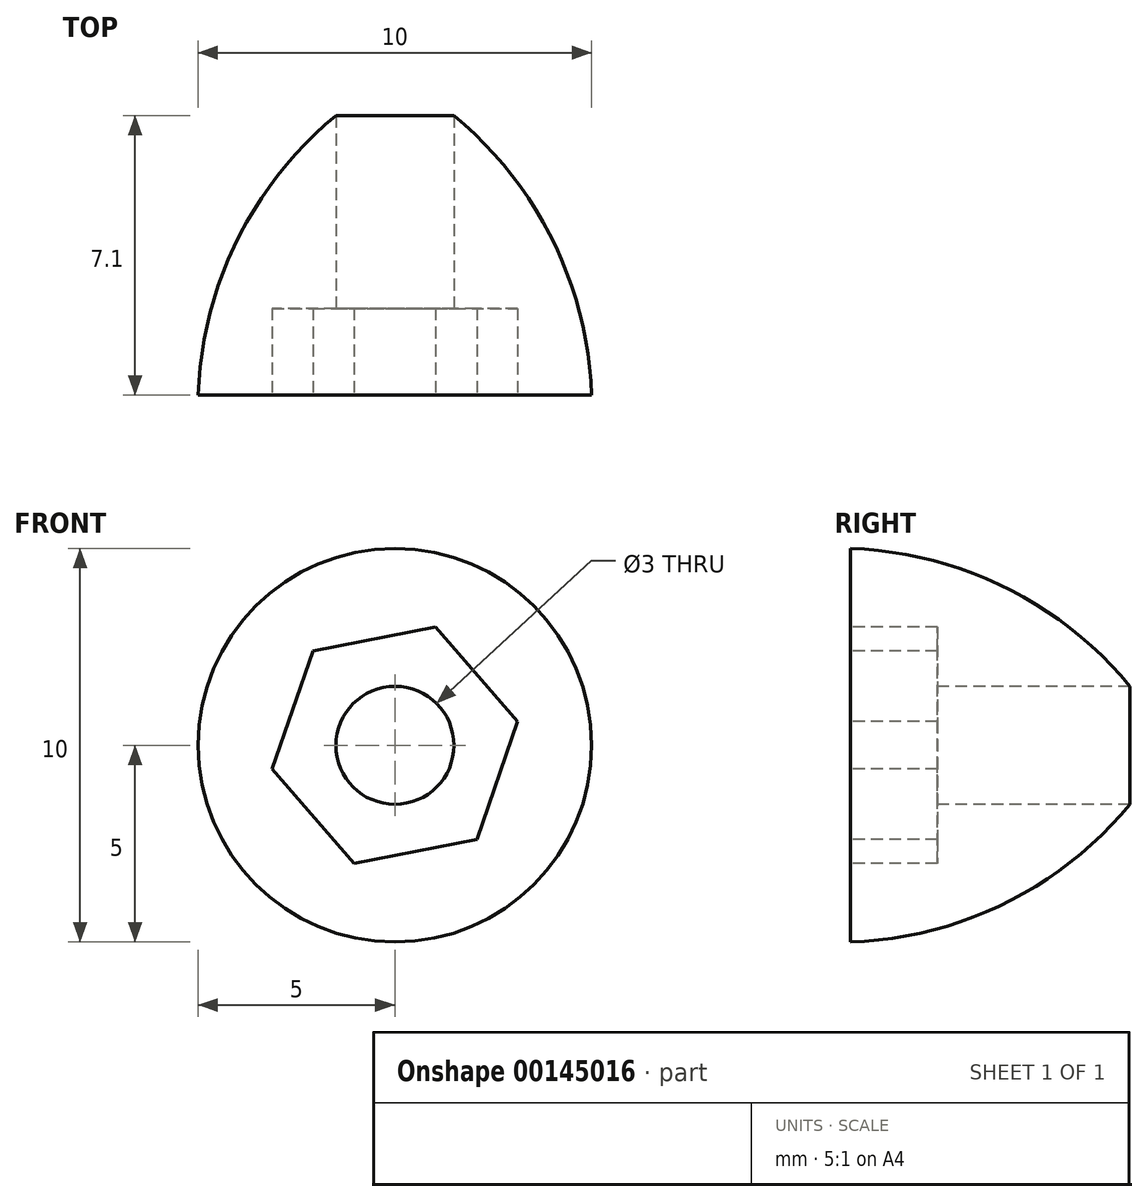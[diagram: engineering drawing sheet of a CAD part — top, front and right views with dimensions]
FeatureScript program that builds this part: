
annotation { "Feature Type Name" : "Feature", "Feature Type Description" : "" }
export const myFeature = defineFeature(function(context is Context, id is Id, definition is map)
    precondition{}
    {
        {
            var Q0;
            Q0=qCreatedBy(makeId("Top.planeOp"),FACE);
            var sketch = newSketch(context, id + "F0", { "sketchPlane" : qUnion([Q0])});
            skLineSegment(sketch, "E0", {"start": v(0, 0) * mm, "end": v(0, 8.12) * mm});
            skLineSegment(sketch, "E1", {"start": v(5, 0) * mm, "end": v(0, 0) * mm});
            skArc(sketch, "E2", {"start": v(5, 0) * mm, "mid": v(3.57, 4.72) * mm, "end": v(0, 8.12) * mm});
            skSolve(sketch);
        }
        {
            var Q0;
            Q0 = qSketchRegion(id + "F0", true);
            var Q1;
            Q1=sQuery(id+"F0.wireOp",EDGE,"E0");
            revolve(context, id + "F1", {"entities" : qUnion([Q0]), "axis" : qUnion([Q1]), "revolveType" : RevolveType.FULL});
        }
        {
            var Q0;
            Q0=makeQuery(id+"F1.opRevolve","SWEPT_FACE",FACE,{"disambiguationData":[OSD([sQuery(id+"F0.wireOp",EDGE,"E1")])]});
            var sketch = newSketch(context, id + "F2", { "sketchPlane" : qUnion([Q0])});
            skCircle(sketch, "E3", {"center": v(0, 0) * mm, "radius": 1.5 * mm});
            skCircle(sketch, "E4.cCircle", {"center": v(0, 0) * mm, "radius": 2.75 * mm, "construction": true});
            skLineSegment(sketch, "E4.0", {"start": v(1.03, 3) * mm, "end": v(3.12, 0.6) * mm});
            skLineSegment(sketch, "E4.1", {"start": v(3.12, 0.6) * mm, "end": v(2.08, -2.4) * mm});
            skLineSegment(sketch, "E4.2", {"start": v(2.08, -2.4) * mm, "end": v(-1.03, -3) * mm});
            skLineSegment(sketch, "E4.3", {"start": v(-1.03, -3) * mm, "end": v(-3.12, -0.6) * mm});
            skLineSegment(sketch, "E4.4", {"start": v(-3.12, -0.6) * mm, "end": v(-2.08, 2.4) * mm});
            skLineSegment(sketch, "E4.5", {"start": v(-2.08, 2.4) * mm, "end": v(1.03, 3) * mm});
            skPoint(sketch, "E4.0.midPoint", {"position": v(2.08, 1.8) * mm});
            skSolve(sketch);
        }
        {
            var Q0;
            Q0=makeQuery(id+"F2.imprint","IMPRINT",FACE,{"disambiguationData":[TD([[makeQuery(id+"F2.imprint","IMPRINT",EDGE,{"derivedFrom":sQuery(id+"F2.wireOp",EDGE,"E3")}),1.0]])]});
            extrude(context, id + "F3", {"entities" : qUnion([Q0]), "operationType" : NewBodyOperationType.REMOVE, "oppositeDirection" : true, "depth" : 25 * mm});
        }
        {
            var Q0;
            Q0 = qSketchRegion(id + "F2", true);
            extrude(context, id + "F4", {"entities" : qUnion([Q0]), "operationType" : NewBodyOperationType.REMOVE, "oppositeDirection" : true, "depth" : 2.2 * mm});
        }
    });
